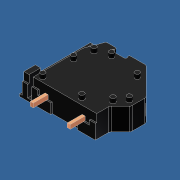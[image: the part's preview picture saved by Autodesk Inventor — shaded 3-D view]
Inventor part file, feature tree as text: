
AUTODESK INVENTOR PART (.ipt)
format: ipt  version: 2012 (Build 160160000, 160)  size: 250,880 bytes
history: native  units: mm (DEFAULTED — no unit token found)
features: sketch x21, extrude x18, revolve x2, pattern_linear x1
ambient origin geometry x8: Origin, YZ Plane, XZ Plane, XY Plane, X Axis, Y Axis, Z Axis, Center Point
bodies: Solid1 (feature_tree)
feature tree (42):
  extrude  "Extrusion1"  Depth=7.5mm TaperAngle=0.0deg
  extrude  "Extrusion2"  Depth=6.6mm TaperAngle=0.0deg
  extrude  "Extrusion3"  Depth=6.3mm TaperAngle=0.0deg
  extrude  "Extrusion4"  Depth=1.5mm TaperAngle=0.0deg
  extrude  "Extrusion5"  Depth=1.5mm TaperAngle=0.0deg
  extrude  "Extrusion6"  Depth=1.5mm TaperAngle=0.0deg
  extrude  "Extrusion7"  Depth=1.5mm TaperAngle=0.0deg
  extrude  "Extrusion8"  Depth=0.5mm TaperAngle=0.0deg
  extrude  "Extrusion9"  Depth=20.0mm TaperAngle=0.0deg
  extrude  "Extrusion10"  TaperAngle=360.0deg  [1 undecoded]
  extrude  "Extrusion11"  [1 undecoded]
  extrude  "Extrusion12"  [1 undecoded]
  extrude  "Extrusion13"  [1 undecoded]
  extrude  "Extrusion14"  [1 undecoded]
  extrude  "Extrusion15"  [1 undecoded]
  extrude  "Extrusion16"  [1 undecoded]
  extrude  "Extrusion17"  [1 undecoded]
  pattern_linear  "Rectangular Pattern1"  [2 undecoded]
  revolve  "Revolution1"  [1 undecoded]
  revolve  "Revolution2"  [1 undecoded]
  extrude  "Extrusion18"  [1 undecoded]
  sketch  "Sketch21"
  sketch  "Skizze_1"  dims[d0=7.5mm d1=0.0mm d2=7.5mm d3=0.0mm]
  sketch  "Skizze_2"  dims[d4=0.8mm d5=0.0mm d6=6.6mm d7=0.0mm]
  sketch  "Skizze_3"  dims[d8=2.8mm d9=0.0mm d10=6.3mm d11=0.0mm]
  sketch  "Skizze_4"  dims[d12=1.5mm d13=0.0mm d14=1.5mm d15=0.0mm]
  sketch  "Skizze_5"  dims[d16=1.5mm d17=0.0mm d18=1.5mm d19=0.0mm]
  sketch  "Skizze_7"  dims[d24=1.5mm d25=0.0mm d26=1.5mm d27=0.0mm]
  sketch  "Skizze_8"  dims[d28=3.5mm d29=0.0mm d30=0.5mm d31=0.0mm]
  sketch  "Skizze_9"  dims[d32=9.0mm d33=0.0mm d34=20.0mm d36=12.5mm d37=10.0mm d39=0.0mm]
  sketch  "Skizze_10"  dims[d40=360.0deg d41=360.0deg]
  sketch  "Skizze_11"  dims[d42=5.8mm d43=0.0mm]
  sketch  "Skizze_12"
  sketch  "Skizze_13"
  sketch  "Skizze_14"
  sketch  "Skizze_15"
  sketch  "Skizze_6"  dims[d20=1.5mm d21=0.0mm d22=1.5mm d23=0.0mm]
  sketch  "Skizze_16"
  sketch  "Skizze_17"
  sketch  "Skizze_19"
  sketch  "Skizze_20"
  sketch  "Skizze_21"
note: 13 required parameter values undecoded (feature->parameter linkage not recoverable at this tier; creation-order binding heuristic only, values carry confidence <= 0.55)
